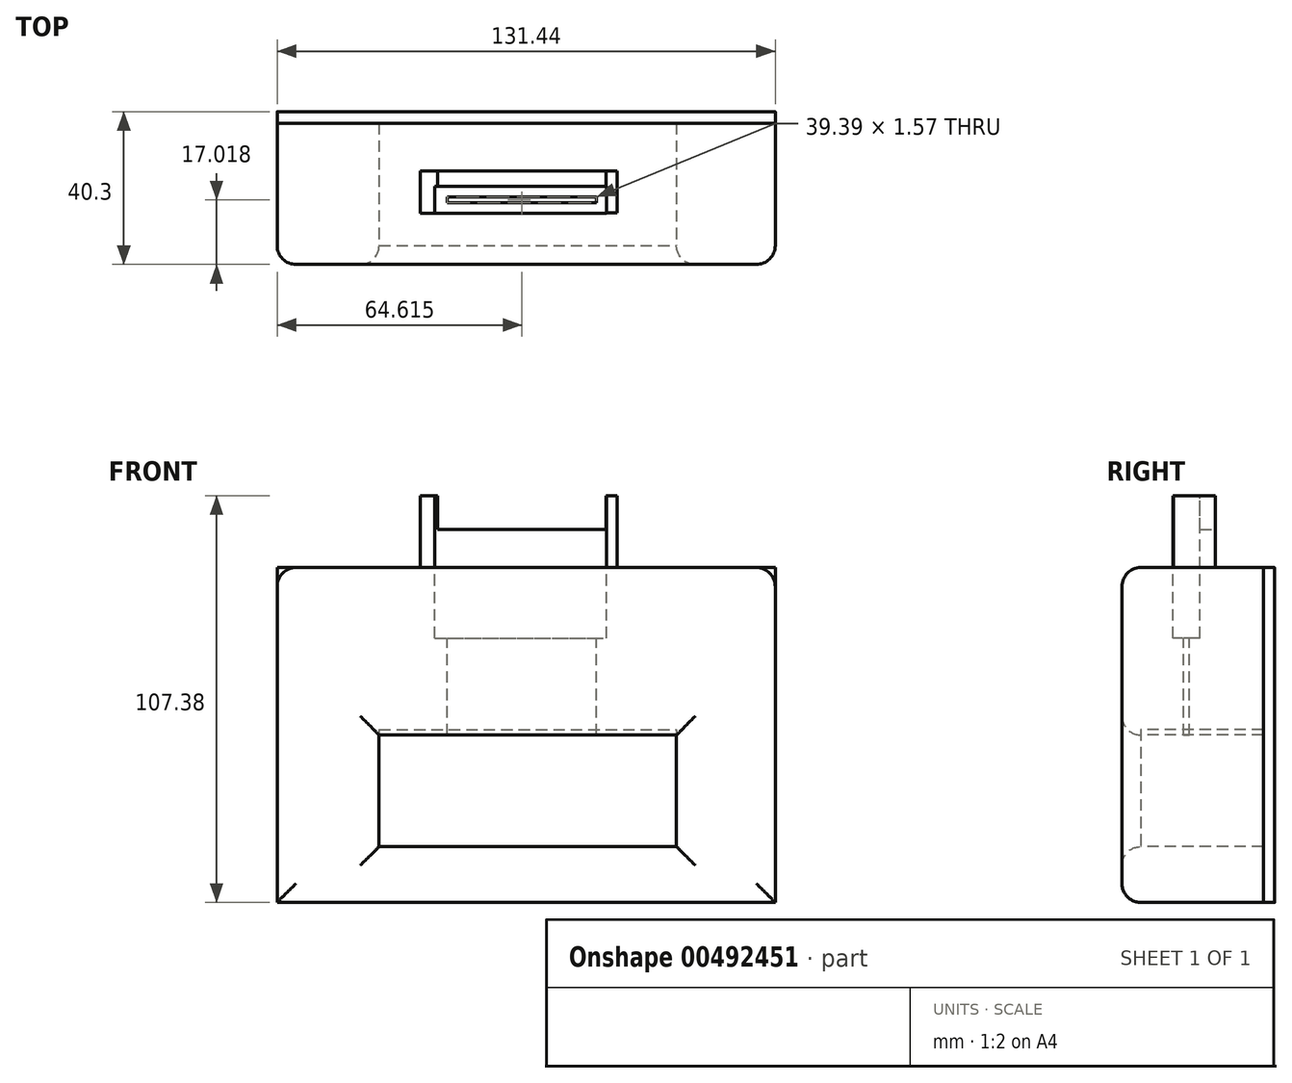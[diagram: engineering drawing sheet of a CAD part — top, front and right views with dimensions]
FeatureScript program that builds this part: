
annotation { "Feature Type Name" : "Feature", "Feature Type Description" : "" }
export const myFeature = defineFeature(function(context is Context, id is Id, definition is map)
    precondition{}
    {
        {
            var Q0;
            Q0=qCreatedBy(makeId("Front.planeOp"),FACE);
            var sketch = newSketch(context, id + "F0", { "sketchPlane" : qUnion([Q0])});
            skLineSegment(sketch, "E0.bottom", {"start": v(65.72, -44.2) * mm, "end": v(-65.72, -44.2) * mm});
            skLineSegment(sketch, "E0.top", {"start": v(65.72, 44.2) * mm, "end": v(-65.72, 44.2) * mm});
            skLineSegment(sketch, "E0.left", {"start": v(65.72, -44.2) * mm, "end": v(65.72, 44.2) * mm});
            skLineSegment(sketch, "E0.right", {"start": v(-65.72, -44.2) * mm, "end": v(-65.72, 44.2) * mm});
            skPoint(sketch, "E0.middle", {"position": v(0, 0) * mm});
            skSolve(sketch);
        }
        {
            var Q0;
            Q0 = qSketchRegion(id + "F0", true);
            extrude(context, id + "F1", {"entities" : qUnion([Q0]), "depth" : 37.3 * mm});
        }
        {
            var Q0;
            Q0=makeQuery(id+"F1.opExtrude","CAP_FACE",FACE,{"disambiguationData":[OSD([sQuery(id+"F0.wireOp",EDGE,"E0.bottom"),sQuery(id+"F0.wireOp",EDGE,"E0.top"),sQuery(id+"F0.wireOp",EDGE,"E0.left"),sQuery(id+"F0.wireOp",EDGE,"E0.right")])],"isStart":false});
            var sketch = newSketch(context, id + "F2", { "sketchPlane" : qUnion([Q0])});
            skLineSegment(sketch, "E1.bottom", {"start": v(-38.8, 0) * mm, "end": v(39.66, 0) * mm});
            skLineSegment(sketch, "E1.top", {"start": v(-38.8, -29.46) * mm, "end": v(39.66, -29.46) * mm});
            skLineSegment(sketch, "E1.left", {"start": v(-38.8, 0) * mm, "end": v(-38.8, -29.46) * mm});
            skLineSegment(sketch, "E1.right", {"start": v(39.66, 0) * mm, "end": v(39.66, -29.46) * mm});
            skSolve(sketch);
        }
        {
            var Q0;
            Q0 = qSketchRegion(id + "F2", true);
            extrude(context, id + "F3", {"entities" : qUnion([Q0]), "operationType" : NewBodyOperationType.REMOVE, "oppositeDirection" : true, "depth" : 61.4 * mm});
        }
        {
            var Q0;
            Q0=makeQuery(id+"F1.opExtrude","CAP_FACE",FACE,{"disambiguationData":[OSD([sQuery(id+"F0.wireOp",EDGE,"E0.bottom"),sQuery(id+"F0.wireOp",EDGE,"E0.top"),sQuery(id+"F0.wireOp",EDGE,"E0.left"),sQuery(id+"F0.wireOp",EDGE,"E0.right")])],"isStart":false});
            fillet(context, id + "F4", {"entities" : qUnion([Q0]), "radius" : 5 * mm, "tangentPropagation" : true, "allowEdgeOverflow" : false});
        }
        {
            var Q0;
            Q0=makeQuery(id+"F1.opExtrude","CAP_FACE",FACE,{"disambiguationData":[OSD([sQuery(id+"F0.wireOp",EDGE,"E0.bottom"),sQuery(id+"F0.wireOp",EDGE,"E0.top"),sQuery(id+"F0.wireOp",EDGE,"E0.left"),sQuery(id+"F0.wireOp",EDGE,"E0.right")])],"isStart":true});
            var sketch = newSketch(context, id + "F5", { "sketchPlane" : qUnion([Q0])});
            skLineSegment(sketch, "E2.bottom", {"start": v(65.72, 44.2) * mm, "end": v(-65.72, 44.2) * mm});
            skLineSegment(sketch, "E2.top", {"start": v(65.72, -44.2) * mm, "end": v(-65.72, -44.2) * mm});
            skLineSegment(sketch, "E2.left", {"start": v(65.72, 44.2) * mm, "end": v(65.72, -44.2) * mm});
            skLineSegment(sketch, "E2.right", {"start": v(-65.72, 44.2) * mm, "end": v(-65.72, -44.2) * mm});
            skSolve(sketch);
        }
        {
            var Q0;
            Q0 = qSketchRegion(id + "F5", true);
            extrude(context, id + "F6", {"entities" : qUnion([Q0]), "depth" : 3 * mm});
        }
        {
            var Q0;
            Q0=makeQuery(id+"F1.opExtrude","SWEPT_FACE",FACE,{"disambiguationData":[OSD([sQuery(id+"F0.wireOp",EDGE,"E0.top")])]});
            var sketch = newSketch(context, id + "F7", { "sketchPlane" : qUnion([Q0])});
            skLineSegment(sketch, "E3.bottom", {"start": v(-24.08, -16.71) * mm, "end": v(21.25, -16.71) * mm});
            skLineSegment(sketch, "E3.top", {"start": v(-24.08, -23.8) * mm, "end": v(21.25, -23.8) * mm});
            skLineSegment(sketch, "E3.left", {"start": v(-24.08, -16.71) * mm, "end": v(-24.08, -23.8) * mm});
            skLineSegment(sketch, "E3.right", {"start": v(21.25, -16.71) * mm, "end": v(21.25, -23.8) * mm});
            skSolve(sketch);
        }
        {
            var Q0;
            Q0=makeQuery(id+"F7.imprint","IMPRINT",FACE,{"disambiguationData":[TD([[makeQuery(id+"F7.imprint","IMPRINT",EDGE,{"derivedFrom":sQuery(id+"F7.wireOp",EDGE,"E3.bottom")}),-1.0]])]});
            extrude(context, id + "F8", {"entities" : qUnion([Q0]), "operationType" : NewBodyOperationType.REMOVE, "oppositeDirection" : true, "depth" : 18.6 * mm});
        }
        {
            var Q0;
            Q0=makeQuery(id+"F8.boolean.opBoolean","COPY",FACE,{"derivedFrom":makeQuery(id+"F8.opExtrude","CAP_FACE",FACE,{"disambiguationData":[OSD([sQuery(id+"F7.wireOp",EDGE,"E3.bottom"),sQuery(id+"F7.wireOp",EDGE,"E3.top"),sQuery(id+"F7.wireOp",EDGE,"E3.left"),sQuery(id+"F7.wireOp",EDGE,"E3.right")])],"isStart":false})});
            var sketch = newSketch(context, id + "F9", { "sketchPlane" : qUnion([Q0])});
            skLineSegment(sketch, "E4.bottom", {"start": v(-20.8, -19.5) * mm, "end": v(18.6, -19.5) * mm});
            skLineSegment(sketch, "E4.top", {"start": v(-20.8, -21.06) * mm, "end": v(18.6, -21.06) * mm});
            skLineSegment(sketch, "E4.left", {"start": v(-20.8, -19.5) * mm, "end": v(-20.8, -21.06) * mm});
            skLineSegment(sketch, "E4.right", {"start": v(18.6, -19.5) * mm, "end": v(18.6, -21.06) * mm});
            skSolve(sketch);
        }
        {
            var Q0;
            Q0 = qSketchRegion(id + "F9", true);
            extrude(context, id + "F10", {"entities" : qUnion([Q0]), "operationType" : NewBodyOperationType.REMOVE, "oppositeDirection" : true, "depth" : 50.6 * mm});
        }
        {
            var Q0;
            Q0=makeQuery(id+"F1.opExtrude","SWEPT_EDGE",EDGE,{"disambiguationData":[OSD([sQuery(id+"F0.wireOp",EDGE,"E0.top"),sQuery(id+"F0.wireOp",EDGE,"E0.left")])]});
            var Q1;
            Q1=makeQuery(id+"F1.opExtrude","SWEPT_EDGE",EDGE,{"disambiguationData":[OSD([sQuery(id+"F0.wireOp",EDGE,"E0.top"),sQuery(id+"F0.wireOp",EDGE,"E0.right")])]});
            fillet(context, id + "F11", {"entities" : qUnion([Q0, Q1]), "radius" : 5 * mm, "tangentPropagation" : true, "allowEdgeOverflow" : false});
        }
        {
            var Q0;
            Q0=makeQuery(id+"F6.opExtrude","CAP_FACE",FACE,{"disambiguationData":[OSD([sQuery(id+"F5.wireOp",EDGE,"E2.bottom"),sQuery(id+"F5.wireOp",EDGE,"E2.top"),sQuery(id+"F5.wireOp",EDGE,"E2.left"),sQuery(id+"F5.wireOp",EDGE,"E2.right")])],"isStart":false});
            var Q1;
            Q1=makeQuery(id+"F6.opExtrude","CAP_EDGE",EDGE,{"disambiguationData":[OSD([sQuery(id+"F5.wireOp",EDGE,"E2.bottom")])],"isStart":false});
            var Q2;
            {var subQ0=sQuery(id+"F0.wireOp",EDGE,"E0.left");var subQ1=sQuery(id+"F0.wireOp",EDGE,"E0.top");Q2=makeQuery(id+"F11.opFillet","BLEND_EDGE",EDGE,{"blendedFrom":[makeQuery(id+"F1.opExtrude","SWEPT_EDGE",EDGE,{"disambiguationData":[OSD([subQ1,subQ0])]}),makeQuery(id+"F1.opExtrude","CAP_FACE",FACE,{"disambiguationData":[OSD([sQuery(id+"F0.wireOp",EDGE,"E0.bottom"),subQ1,subQ0,sQuery(id+"F0.wireOp",EDGE,"E0.right")])],"isStart":true})],"blendedInto":[makeQuery(id+"F1.opExtrude","CAP_FACE",FACE,{"disambiguationData":[OSD([sQuery(id+"F0.wireOp",EDGE,"E0.bottom"),subQ1,subQ0,sQuery(id+"F0.wireOp",EDGE,"E0.right")])],"isStart":true})]});}
            var Q3;
            {var subQ0=sQuery(id+"F0.wireOp",EDGE,"E0.right");var subQ1=sQuery(id+"F0.wireOp",EDGE,"E0.top");Q3=makeQuery(id+"F11.opFillet","BLEND_EDGE",EDGE,{"blendedFrom":[makeQuery(id+"F1.opExtrude","SWEPT_EDGE",EDGE,{"disambiguationData":[OSD([subQ1,subQ0])]}),makeQuery(id+"F1.opExtrude","CAP_FACE",FACE,{"disambiguationData":[OSD([sQuery(id+"F0.wireOp",EDGE,"E0.bottom"),subQ1,sQuery(id+"F0.wireOp",EDGE,"E0.left"),subQ0])],"isStart":true})],"blendedInto":[makeQuery(id+"F1.opExtrude","CAP_FACE",FACE,{"disambiguationData":[OSD([sQuery(id+"F0.wireOp",EDGE,"E0.bottom"),subQ1,sQuery(id+"F0.wireOp",EDGE,"E0.left"),subQ0])],"isStart":true})]});}
            fillet(context, id + "F12", {"entities" : qUnion([Q0, Q1, Q2, Q3]), "radius" : 0.02 * mm, "tangentPropagation" : true, "allowEdgeOverflow" : false});
        }
        {
            var Q0;
            Q0=makeQuery(id+"F1.opExtrude","SWEPT_FACE",FACE,{"disambiguationData":[OSD([sQuery(id+"F0.wireOp",EDGE,"E0.top")])]});
            var sketch = newSketch(context, id + "F13", { "sketchPlane" : qUnion([Q0])});
            skLineSegment(sketch, "E5.bottom", {"start": v(-24.08, -16.71) * mm, "end": v(21.25, -16.71) * mm});
            skLineSegment(sketch, "E5.top", {"start": v(-24.08, -12.61) * mm, "end": v(21.25, -12.61) * mm});
            skLineSegment(sketch, "E5.left", {"start": v(-24.08, -16.71) * mm, "end": v(-24.08, -12.61) * mm});
            skLineSegment(sketch, "E5.right", {"start": v(21.25, -16.71) * mm, "end": v(21.25, -12.61) * mm});
            skSolve(sketch);
        }
        {
            var Q0;
            Q0 = qSketchRegion(id + "F13", true);
            extrude(context, id + "F14", {"entities" : qUnion([Q0]), "operationType" : NewBodyOperationType.ADD, "depth" : 19 * mm});
        }
        {
            var Q0;
            Q0=makeQuery(id+"F1.opExtrude","SWEPT_FACE",FACE,{"disambiguationData":[OSD([sQuery(id+"F0.wireOp",EDGE,"E0.top")])]});
            var sketch = newSketch(context, id + "F15", { "sketchPlane" : qUnion([Q0])});
            skLineSegment(sketch, "E6.bottom", {"start": v(-24.08, -12.61) * mm, "end": v(-27.88, -12.61) * mm});
            skLineSegment(sketch, "E6.top", {"start": v(-24.08, -23.8) * mm, "end": v(-27.88, -23.8) * mm});
            skLineSegment(sketch, "E6.left", {"start": v(-24.08, -12.61) * mm, "end": v(-24.08, -23.8) * mm});
            skLineSegment(sketch, "E6.right", {"start": v(-27.88, -12.61) * mm, "end": v(-27.88, -23.8) * mm});
            skSolve(sketch);
        }
        {
            var Q0;
            Q0 = qSketchRegion(id + "F15", true);
            extrude(context, id + "F16", {"entities" : qUnion([Q0]), "operationType" : NewBodyOperationType.ADD, "depth" : 19 * mm});
        }
        {
            var Q0;
            Q0=makeQuery(id+"F1.opExtrude","SWEPT_FACE",FACE,{"disambiguationData":[OSD([sQuery(id+"F0.wireOp",EDGE,"E0.top")])]});
            var sketch = newSketch(context, id + "F17", { "sketchPlane" : qUnion([Q0])});
            skLineSegment(sketch, "E7.bottom", {"start": v(21.25, -12.61) * mm, "end": v(24.01, -12.61) * mm});
            skLineSegment(sketch, "E7.top", {"start": v(21.25, -23.63) * mm, "end": v(24.01, -23.63) * mm});
            skLineSegment(sketch, "E7.left", {"start": v(21.25, -12.61) * mm, "end": v(21.25, -23.63) * mm});
            skLineSegment(sketch, "E7.right", {"start": v(24.01, -12.61) * mm, "end": v(24.01, -23.63) * mm});
            skSolve(sketch);
        }
        {
            var Q0;
            Q0 = qSketchRegion(id + "F17", true);
            extrude(context, id + "F18", {"entities" : qUnion([Q0]), "operationType" : NewBodyOperationType.ADD, "depth" : 19 * mm});
        }
        {
            var Q0;
            Q0=makeQuery(id+"F18.boolean.opBoolean","MERGE",FACE,{"derivedFrom":[makeQuery(id+"F16.boolean.opBoolean","MERGE",FACE,{"derivedFrom":[makeQuery(id+"F14.opExtrude","SWEPT_FACE",FACE,{"disambiguationData":[OSD([sQuery(id+"F13.wireOp",EDGE,"E5.top")])]}),makeQuery(id+"F16.opExtrude","SWEPT_FACE",FACE,{"disambiguationData":[OSD([sQuery(id+"F15.wireOp",EDGE,"E6.bottom")])]})]}),makeQuery(id+"F18.opExtrude","SWEPT_FACE",FACE,{"disambiguationData":[OSD([sQuery(id+"F17.wireOp",EDGE,"E7.bottom")])]})]});
            var sketch = newSketch(context, id + "F19", { "sketchPlane" : qUnion([Q0])});
            skLineSegment(sketch, "E8.bottom", {"start": v(23.34, 63.2) * mm, "end": v(-21.04, 63.2) * mm});
            skLineSegment(sketch, "E8.top", {"start": v(23.34, 54.25) * mm, "end": v(-21.04, 54.25) * mm});
            skLineSegment(sketch, "E8.left", {"start": v(23.34, 63.2) * mm, "end": v(23.34, 54.25) * mm});
            skLineSegment(sketch, "E8.right", {"start": v(-21.04, 63.2) * mm, "end": v(-21.04, 54.25) * mm});
            skSolve(sketch);
        }
        {
            var Q0;
            Q0 = qSketchRegion(id + "F19", true);
            extrude(context, id + "F20", {"entities" : qUnion([Q0]), "operationType" : NewBodyOperationType.REMOVE, "oppositeDirection" : true, "depth" : 25 * mm});
        }
        {
            var Q0;
            Q0=makeQuery(id+"F3.boolean.opBoolean","COPY",FACE,{"derivedFrom":makeQuery(id+"F3.opExtrude","SWEPT_FACE",FACE,{"disambiguationData":[OSD([sQuery(id+"F2.wireOp",EDGE,"E1.top")])]})});
            extrude(context, id + "F21", {"entities" : qUnion([Q0]), "depth" : 30.9 * mm});
        }
    });
